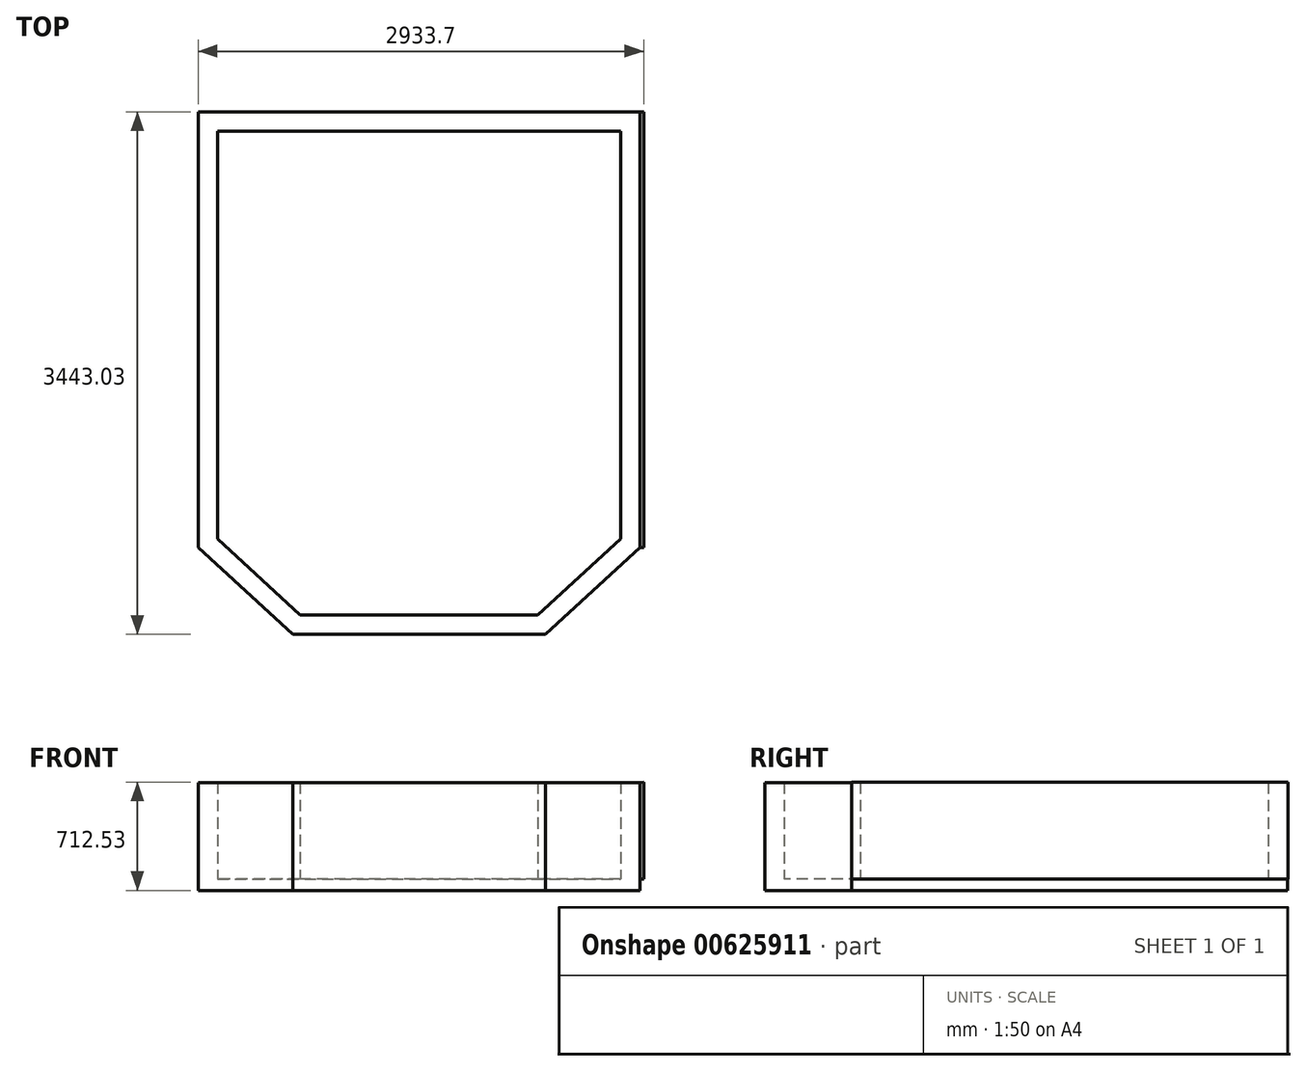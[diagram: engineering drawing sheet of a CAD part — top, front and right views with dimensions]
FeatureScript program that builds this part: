
annotation { "Feature Type Name" : "Feature", "Feature Type Description" : "" }
export const myFeature = defineFeature(function(context is Context, id is Id, definition is map)
    precondition{}
    {
        {
            var Q0;
            Q0=qCreatedBy(makeId("Top.planeOp"),FACE);
            var sketch = newSketch(context, id + "F0", { "sketchPlane" : qUnion([Q0])});
            skLineSegment(sketch, "E0", {"start": v(0, 0) * mm, "end": v(2908.3, 0) * mm});
            skLineSegment(sketch, "E1", {"start": v(2908.3, 0) * mm, "end": v(2908.3, -2870.2) * mm});
            skLineSegment(sketch, "E2", {"start": v(2908.3, -2870.2) * mm, "end": v(2286, -3441.7) * mm});
            skLineSegment(sketch, "E3", {"start": v(2286, -3441.7) * mm, "end": v(622.3, -3441.7) * mm});
            skLineSegment(sketch, "E4", {"start": v(622.3, -3441.7) * mm, "end": v(0, -2870.2) * mm});
            skLineSegment(sketch, "E5", {"start": v(0, -2870.2) * mm, "end": v(0, 0) * mm});
            skLineSegment(sketch, "E6.0", {"start": v(127, -2814.4) * mm, "end": v(127, -127) * mm});
            skLineSegment(sketch, "E6.1", {"start": v(2781.3, -127) * mm, "end": v(2781.3, -2814.4) * mm});
            skLineSegment(sketch, "E6.2", {"start": v(2781.3, -2814.4) * mm, "end": v(2236.53, -3314.7) * mm});
            skLineSegment(sketch, "E6.3", {"start": v(127, -127) * mm, "end": v(2781.3, -127) * mm});
            skLineSegment(sketch, "E6.4", {"start": v(2236.53, -3314.7) * mm, "end": v(671.77, -3314.7) * mm});
            skLineSegment(sketch, "E6.5", {"start": v(671.77, -3314.7) * mm, "end": v(127, -2814.4) * mm});
            skSolve(sketch);
        }
        {
            var Q0;
            Q0=makeQuery(id+"F0.imprint","IMPRINT",FACE,{"disambiguationData":[TD([[makeQuery(id+"F0.imprint","IMPRINT",EDGE,{"derivedFrom":sQuery(id+"F0.wireOp",EDGE,"E0")}),-1.0]])]});
            var Q1;
            Q1=makeQuery(id+"F0.imprint","IMPRINT",FACE,{"disambiguationData":[TD([[makeQuery(id+"F0.imprint","IMPRINT",EDGE,{"derivedFrom":sQuery(id+"F0.wireOp",EDGE,"E6.0")}),-1.0]])]});
            extrude(context, id + "F1", {"entities" : qUnion([Q0, Q1]), "oppositeDirection" : true, "depth" : 76.2 * mm, "offsetDistance" : 25.4 * mm});
        }
        {
            var Q0;
            Q0=makeQuery(id+"F0.imprint","IMPRINT",FACE,{"disambiguationData":[TD([[makeQuery(id+"F0.imprint","IMPRINT",EDGE,{"derivedFrom":sQuery(id+"F0.wireOp",EDGE,"E0")}),-1.0]])]});
            extrude(context, id + "F2", {"entities" : qUnion([Q0]), "depth" : 635 * mm, "offsetDistance" : 25.4 * mm});
        }
        {
            var Q0;
            Q0=makeQuery(id+"F2.opExtrude","SWEPT_FACE",FACE,{"disambiguationData":[OSD([sQuery(id+"F0.wireOp",EDGE,"E1")])]});
            extrude(context, id + "F3", {"entities" : qUnion([Q0]), "operationType" : NewBodyOperationType.ADD, "depth" : 25.4 * mm, "offsetDistance" : 25.4 * mm, "hasDraft" : true, "draftAngle" : 3 * degree});
        }
    });
